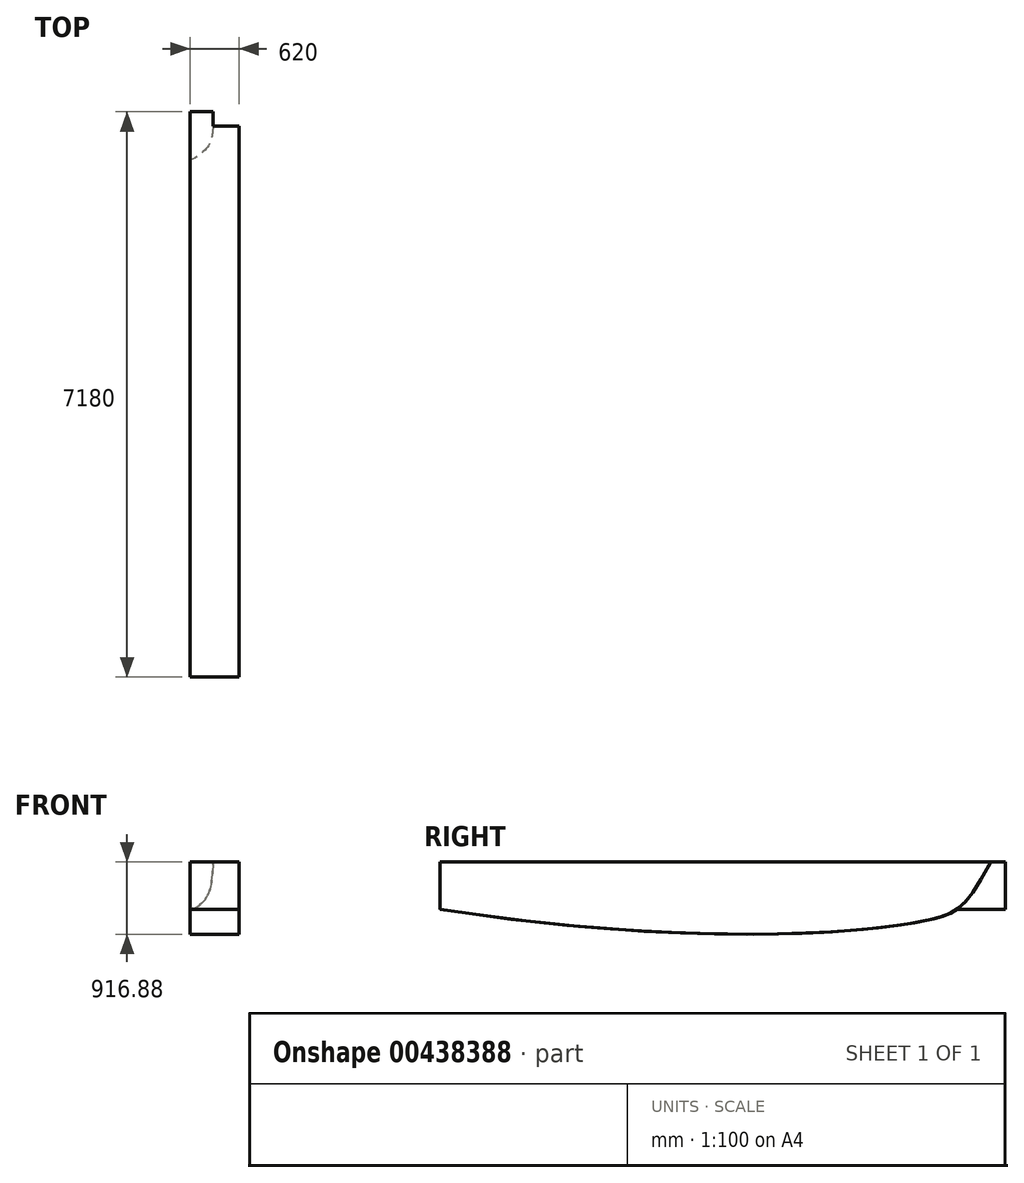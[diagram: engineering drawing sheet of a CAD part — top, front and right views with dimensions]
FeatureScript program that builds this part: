
annotation { "Feature Type Name" : "Feature", "Feature Type Description" : "" }
export const myFeature = defineFeature(function(context is Context, id is Id, definition is map)
    precondition{}
    {
        {
            var Q0;
            Q0=qCreatedBy(makeId("Right.planeOp"),FACE);
            var sketch = newSketch(context, id + "F0", { "sketchPlane" : qUnion([Q0])});
            skLineSegment(sketch, "E0", {"start": v(0, 0) * mm, "end": v(7000, 0) * mm});
            skLineSegment(sketch, "E1", {"start": v(0, 0) * mm, "end": v(0, -600) * mm});
            skFitSpline(sketch, "E2", {"points": [v(7000, 0) * mm, v(6268.78, -721.14) * mm, v(0, -600) * mm], "startDerivative": vector(-3261.65, -5710) * mm, "endDerivative": vector(-12934.08, 2020.77) * mm});
            skSolve(sketch);
        }
        {
            var Q0;
            Q0=qCreatedBy(makeId("Front.planeOp"),FACE);
            var sketch = newSketch(context, id + "F1", { "sketchPlane" : qUnion([Q0])});
            skFitSpline(sketch, "E3", {"points": [v(0, -600.6) * mm, v(207.08, -449.87) * mm, v(290.9, 0) * mm], "startDerivative": vector(767.02, 193.58) * mm, "endDerivative": vector(54.92, 1398.04) * mm});
            skLineSegment(sketch, "E4", {"start": v(0, 0) * mm, "end": v(0, -600.6) * mm});
            skFitSpline(sketch, "E5.MirrorCS", {"points": [v(0, -600.6) * mm, v(-207.08, -449.87) * mm, v(-290.9, 0) * mm], "startDerivative": vector(-767.02, 193.58) * mm, "endDerivative": vector(-54.92, 1398.04) * mm});
            skLineSegment(sketch, "E6", {"start": v(-290.9, 0) * mm, "end": v(290.9, 0) * mm});
            skSolve(sketch);
        }
        {
            var Q0;
            Q0=makeQuery(id+"F0.imprint","IMPRINT",FACE,{"disambiguationData":[TD([[makeQuery(id+"F0.imprint","IMPRINT",EDGE,{"derivedFrom":sQuery(id+"F0.wireOp",EDGE,"E0")}),-1.0]])]});
            extrude(context, id + "F2", {"entities" : qUnion([Q0]), "depth" : 430 * mm});
        }
        {
            var Q0;
            {var subQ0=sQuery(id+"F1.wireOp",EDGE,"E3");Q0=makeQuery(id+"F1.imprint","IMPRINT",FACE,{"disambiguationData":[TD([[makeQuery(id+"F1.imprint","IMPRINT",EDGE,{"derivedFrom":subQ0}),1.0]])]});}
            extrude(context, id + "F3", {"entities" : qUnion([Q0]), "operationType" : NewBodyOperationType.ADD, "oppositeDirection" : true, "depth" : 7180 * mm});
        }
        {
            var Q0;
            Q0=makeQuery(id+"F2.opExtrude","CAP_FACE",FACE,{"disambiguationData":[OSD([sQuery(id+"F0.wireOp",EDGE,"E0"),sQuery(id+"F0.wireOp",EDGE,"E1"),sQuery(id+"F0.wireOp",EDGE,"E2")])],"isStart":false});
            extrude(context, id + "F4", {"entities" : qUnion([Q0]), "operationType" : NewBodyOperationType.ADD, "depth" : 190 * mm});
        }
    });
